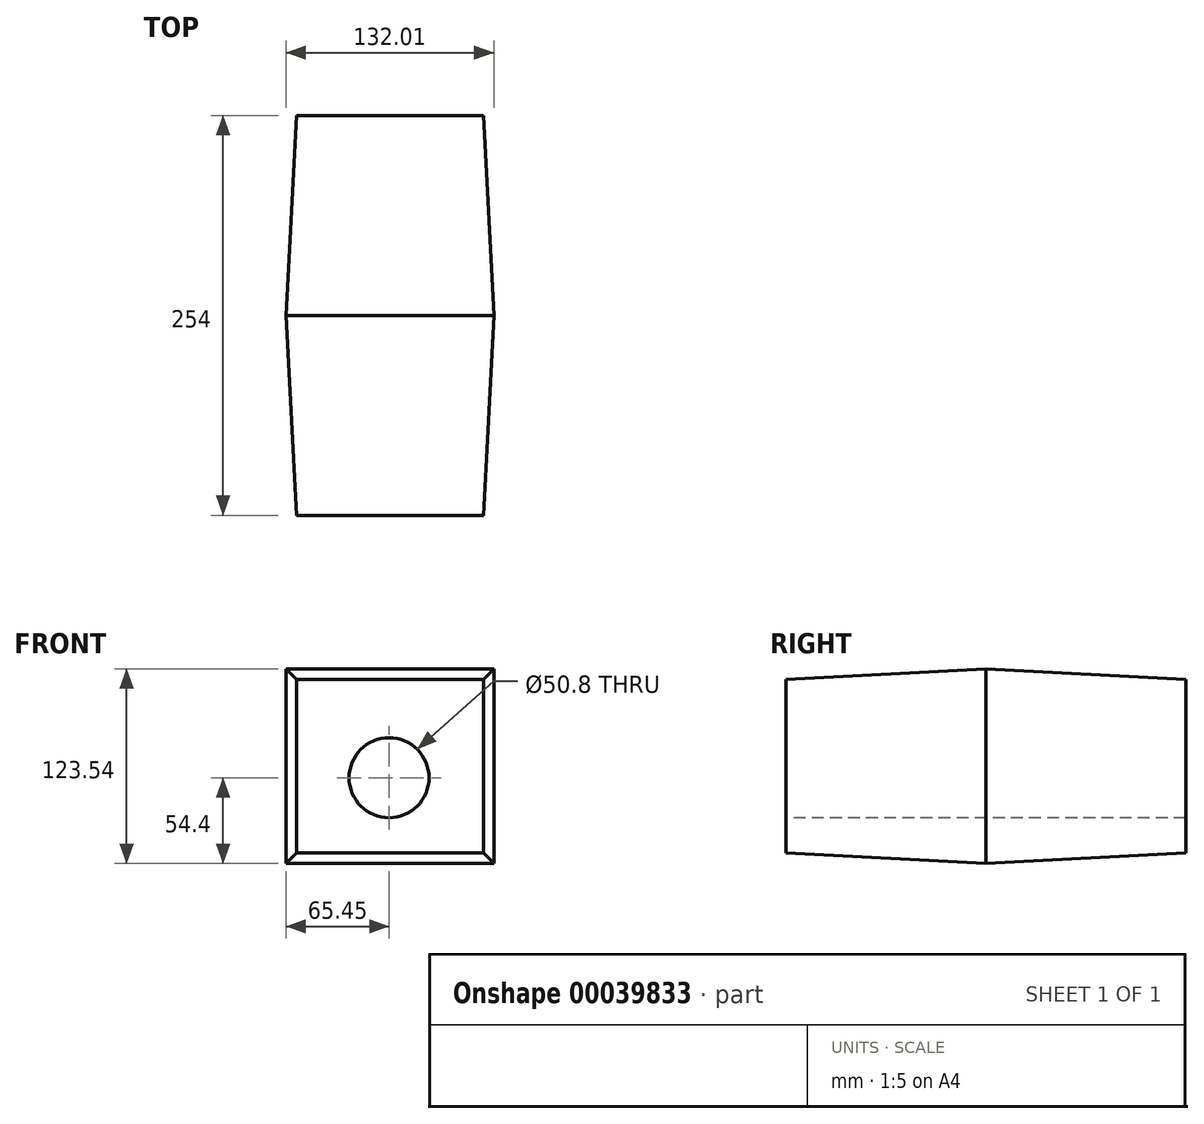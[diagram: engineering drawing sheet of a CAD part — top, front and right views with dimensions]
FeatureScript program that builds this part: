
annotation { "Feature Type Name" : "Feature", "Feature Type Description" : "" }
export const myFeature = defineFeature(function(context is Context, id is Id, definition is map)
    precondition{}
    {
        {
            var Q0;
            Q0=qCreatedBy(makeId("Front.planeOp"),FACE);
            var sketch = newSketch(context, id + "F0", { "sketchPlane" : qUnion([Q0])});
            skLineSegment(sketch, "E0.bottom", {"start": v(66.56, 69.14) * mm, "end": v(-65.45, 69.14) * mm});
            skLineSegment(sketch, "E0.top", {"start": v(66.56, -54.4) * mm, "end": v(-65.45, -54.4) * mm});
            skLineSegment(sketch, "E0.left", {"start": v(66.56, 69.14) * mm, "end": v(66.56, -54.4) * mm});
            skLineSegment(sketch, "E0.right", {"start": v(-65.45, 69.14) * mm, "end": v(-65.45, -54.4) * mm});
            skSolve(sketch);
        }
        {
            var Q0;
            Q0=makeQuery(id+"F0.imprint","IMPRINT",FACE,{"disambiguationData":[TD([[makeQuery(id+"F0.imprint","IMPRINT",EDGE,{"derivedFrom":sQuery(id+"F0.wireOp",EDGE,"E0.bottom")}),1.0]])]});
            extrude(context, id + "F1", {"entities" : qUnion([Q0]), "depth" : 127 * mm, "hasDraft" : true, "draftAngle" : 3 * degree, "draftPullDirection" : true, "hasSecondDirection" : true, "secondDirectionOppositeDirection" : true, "secondDirectionDepth" : 127 * mm, "hasSecondDirectionDraft" : true, "secondDirectionDraftAngle" : 3 * degree, "secondDirectionDraftPullDirection" : true});
        }
        {
            var Q0;
            Q0=makeQuery(id+"F1.opExtrude","CAP_FACE",FACE,{"disambiguationData":[OSD([sQuery(id+"F0.wireOp",EDGE,"E0.bottom"),sQuery(id+"F0.wireOp",EDGE,"E0.top"),sQuery(id+"F0.wireOp",EDGE,"E0.left"),sQuery(id+"F0.wireOp",EDGE,"E0.right")])],"isStart":false});
            var sketch = newSketch(context, id + "F2", { "sketchPlane" : qUnion([Q0])});
            skPoint(sketch, "E1", {"position": v(0, 0) * mm});
            skSolve(sketch);
        }
        {
            var Q0;
            Q0=sQuery(id+"F2.wireOp",VERTEX,"E1");
            var Q1;
            Q1=makeQuery(id+"F1.split0.splitOp","SPLIT",BODY,{"derivedFrom":makeQuery(id+"F1.opExtrude","SWEPT_BODY",BODY,{"disambiguationData":[OSD([sQuery(id+"F0.wireOp",EDGE,"E0.bottom"),sQuery(id+"F0.wireOp",EDGE,"E0.top"),sQuery(id+"F0.wireOp",EDGE,"E0.left"),sQuery(id+"F0.wireOp",EDGE,"E0.right")])]})});
            hole(context, id + "F3", {"style" : HoleStyle.SIMPLE, "holeDiameter" : 50.8 * mm, "endStyle" : HoleEndStyle.THROUGH, "locations" : qUnion([Q0]), "scope" : qUnion([Q1])});
        }
    });
